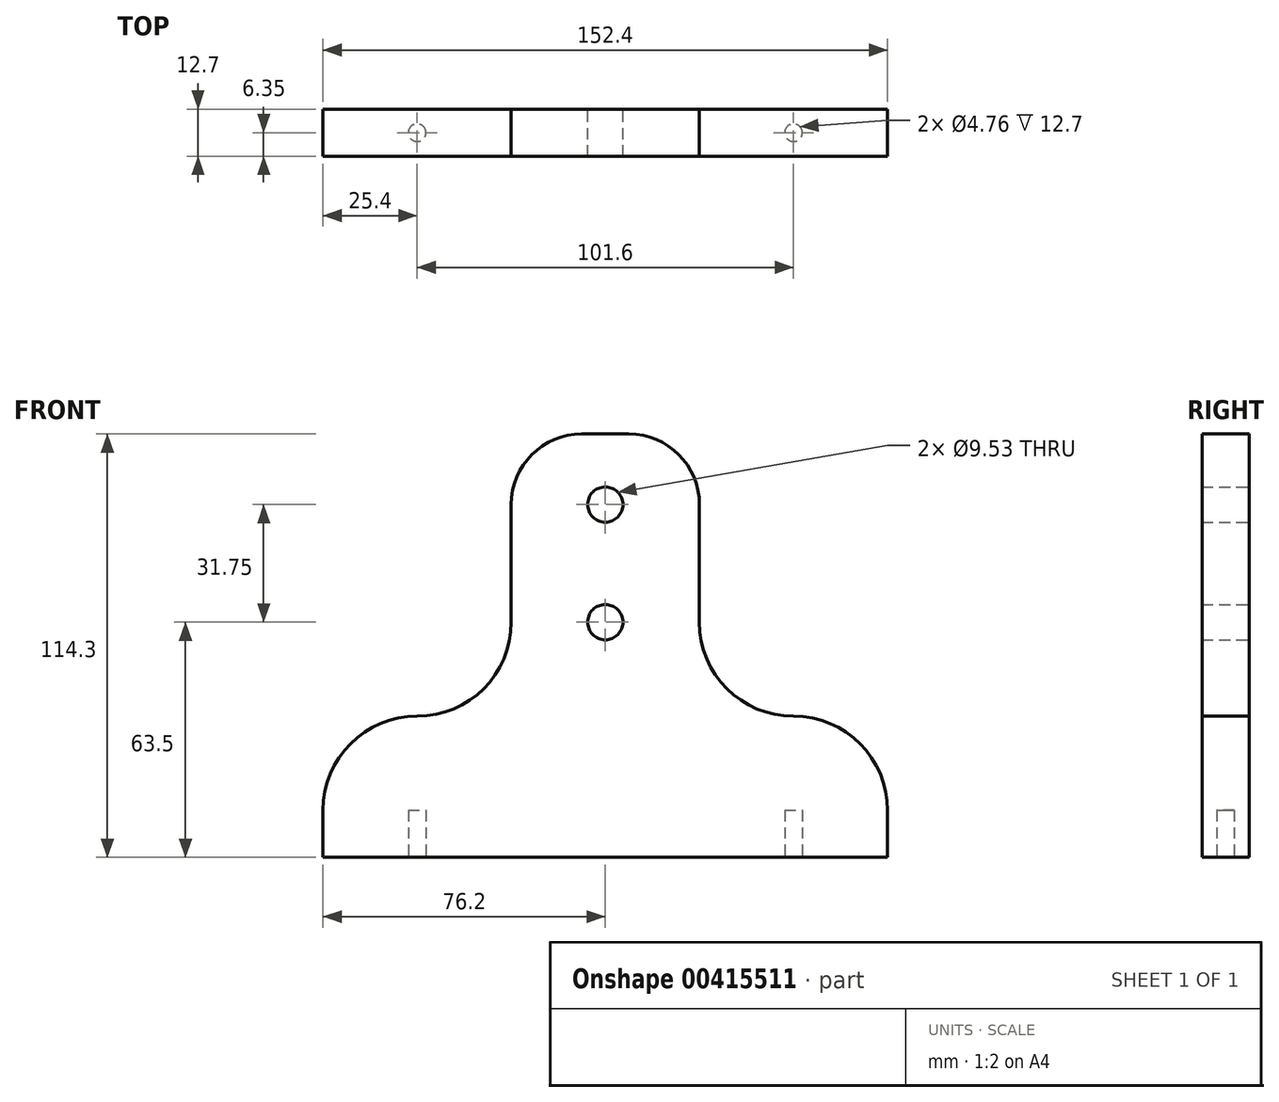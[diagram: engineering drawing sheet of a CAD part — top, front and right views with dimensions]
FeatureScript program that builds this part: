
annotation { "Feature Type Name" : "Feature", "Feature Type Description" : "" }
export const myFeature = defineFeature(function(context is Context, id is Id, definition is map)
    precondition{}
    {
        {
            var Q0;
            Q0=qCreatedBy(makeId("Front.planeOp"),FACE);
            var sketch = newSketch(context, id + "F0", { "sketchPlane" : qUnion([Q0])});
            skLineSegment(sketch, "E0", {"start": v(-76.2, 0) * mm, "end": v(76.2, 0) * mm});
            skLineSegment(sketch, "E1", {"start": v(76.2, 0) * mm, "end": v(76.2, 12.7) * mm});
            skLineSegment(sketch, "E2", {"start": v(50.8, 38.1) * mm, "end": v(50.8, 38.1) * mm});
            skLineSegment(sketch, "E3", {"start": v(25.4, 63.5) * mm, "end": v(25.4, 95.25) * mm});
            skLineSegment(sketch, "E4", {"start": v(6.35, 114.3) * mm, "end": v(-6.35, 114.3) * mm});
            skLineSegment(sketch, "E5", {"start": v(-25.4, 95.25) * mm, "end": v(-25.4, 63.5) * mm});
            skLineSegment(sketch, "E6", {"start": v(-50.8, 38.1) * mm, "end": v(-50.8, 38.1) * mm});
            skLineSegment(sketch, "E7", {"start": v(-76.2, 12.7) * mm, "end": v(-76.2, 0) * mm});
            skCircle(sketch, "E8", {"center": v(0, 95.25) * mm, "radius": 4.76 * mm});
            skCircle(sketch, "E9", {"center": v(0, 63.5) * mm, "radius": 4.76 * mm});
            skLineSegment(sketch, "E10", {"start": v(0, 114.3) * mm, "end": v(0, 0) * mm, "construction": true});
            skPoint(sketch, "E11.visualSharp", {"position": v(-25.4, 38.1) * mm});
            skArc(sketch, "E11.filletArc", {"start": v(-50.8, 38.1) * mm, "mid": v(-32.84, 45.54) * mm, "end": v(-25.4, 63.5) * mm});
            skPoint(sketch, "E12.visualSharp", {"position": v(25.4, 38.1) * mm});
            skArc(sketch, "E12.filletArc", {"start": v(25.4, 63.5) * mm, "mid": v(32.84, 45.54) * mm, "end": v(50.8, 38.1) * mm});
            skPoint(sketch, "E13.visualSharp", {"position": v(-76.2, 38.1) * mm});
            skArc(sketch, "E13.filletArc", {"start": v(-50.8, 38.1) * mm, "mid": v(-68.76, 30.66) * mm, "end": v(-76.2, 12.7) * mm});
            skPoint(sketch, "E14.visualSharp", {"position": v(76.2, 38.1) * mm});
            skArc(sketch, "E14.filletArc", {"start": v(76.2, 12.7) * mm, "mid": v(68.76, 30.66) * mm, "end": v(50.8, 38.1) * mm});
            skPoint(sketch, "E15.visualSharp", {"position": v(-25.4, 114.3) * mm});
            skArc(sketch, "E15.filletArc", {"start": v(-6.35, 114.3) * mm, "mid": v(-19.82, 108.72) * mm, "end": v(-25.4, 95.25) * mm});
            skPoint(sketch, "E16.visualSharp", {"position": v(25.4, 114.3) * mm});
            skArc(sketch, "E16.filletArc", {"start": v(25.4, 95.25) * mm, "mid": v(19.82, 108.72) * mm, "end": v(6.35, 114.3) * mm});
            skSolve(sketch);
        }
        {
            var Q0;
            Q0=qSketchRegion(id+"F0",true);
            extrude(context, id + "F1", {"entities" : qUnion([Q0]), "depth" : 12.7 * mm});
        }
        {
            var Q0;
            Q0=makeQuery(id+"F1.opExtrude","SWEPT_FACE",FACE,{"disambiguationData":[OSD([sQuery(id+"F0.wireOp",EDGE,"E0")])]});
            var sketch = newSketch(context, id + "F2", { "sketchPlane" : qUnion([Q0])});
            skCircle(sketch, "E17", {"center": v(-50.8, 6.35) * mm, "radius": 2.38 * mm});
            skCircle(sketch, "E18", {"center": v(50.8, 6.35) * mm, "radius": 2.38 * mm});
            skLineSegment(sketch, "E19", {"start": v(-50.8, 6.35) * mm, "end": v(50.8, 6.35) * mm, "construction": true});
            skLineSegment(sketch, "E20", {"start": v(0, 0) * mm, "end": v(0, 6.35) * mm, "construction": true});
            skLineSegment(sketch, "E21", {"start": v(0, 6.35) * mm, "end": v(0, 12.7) * mm, "construction": true});
            skSolve(sketch);
        }
        {
            var Q0;
            Q0=qSketchRegion(id+"F2",true);
            extrude(context, id + "F3", {"entities" : qUnion([Q0]), "operationType" : NewBodyOperationType.REMOVE, "oppositeDirection" : true, "depth" : 12.7 * mm});
        }
    });
